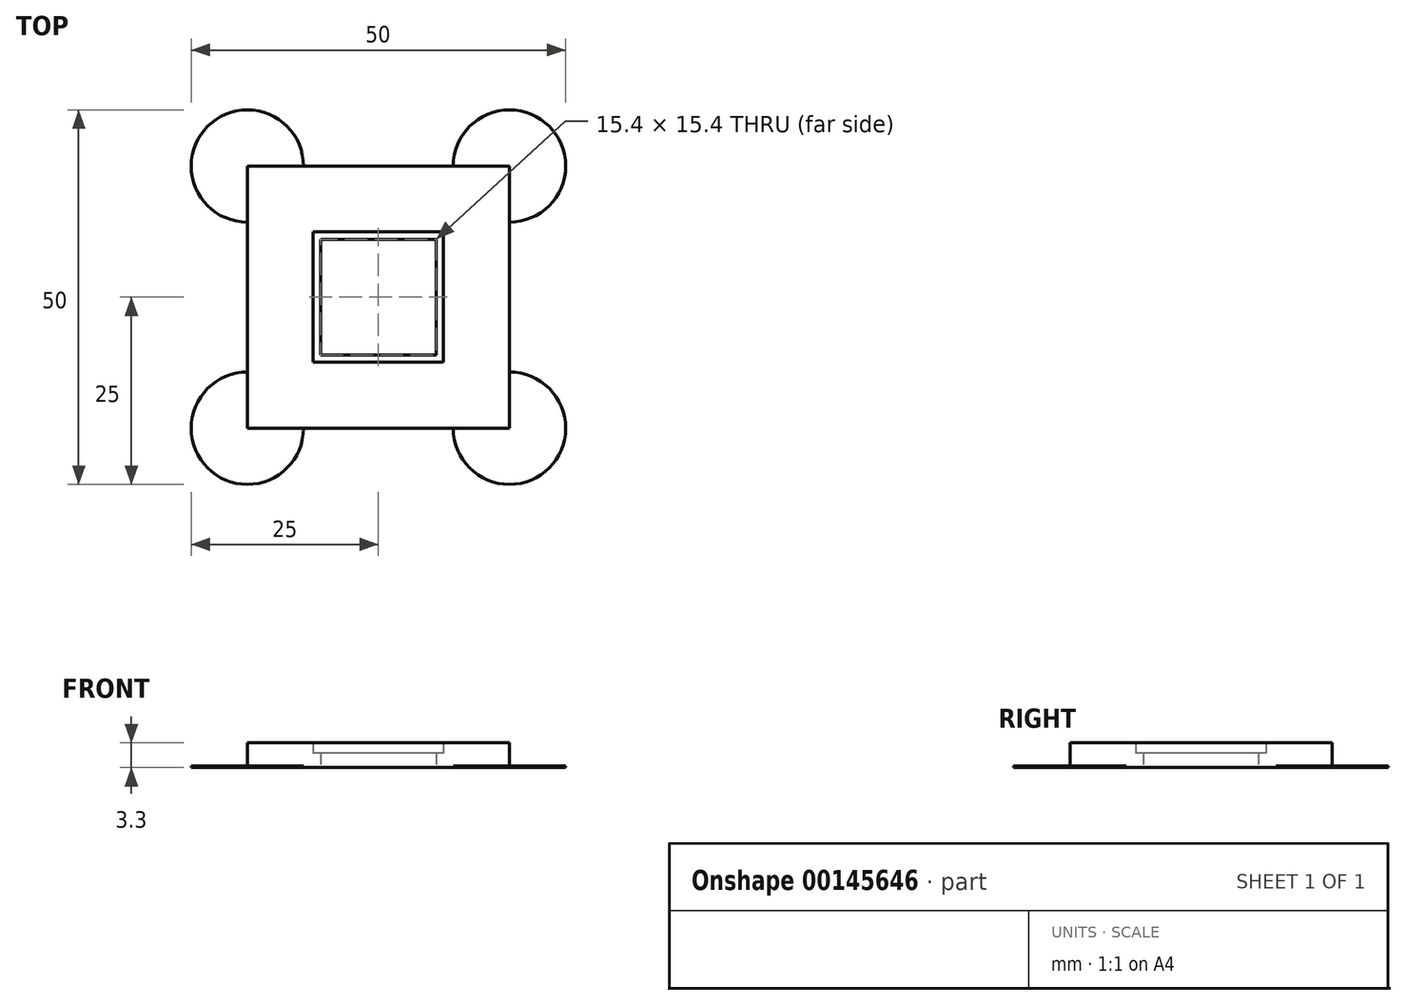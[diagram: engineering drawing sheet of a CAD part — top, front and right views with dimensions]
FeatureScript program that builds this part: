
annotation { "Feature Type Name" : "Feature", "Feature Type Description" : "" }
export const myFeature = defineFeature(function(context is Context, id is Id, definition is map)
    precondition{}
    {
        {
            var Q0;
            Q0=qCreatedBy(makeId("Top.planeOp"),FACE);
            var sketch = newSketch(context, id + "F0", { "sketchPlane" : qUnion([Q0])});
            skLineSegment(sketch, "E0.bottom", {"start": v(17.5, 17.5) * mm, "end": v(-17.5, 17.5) * mm});
            skLineSegment(sketch, "E0.top", {"start": v(17.5, -17.5) * mm, "end": v(-17.5, -17.5) * mm});
            skLineSegment(sketch, "E0.left", {"start": v(17.5, 17.5) * mm, "end": v(17.5, -17.5) * mm});
            skLineSegment(sketch, "E0.right", {"start": v(-17.5, 17.5) * mm, "end": v(-17.5, -17.5) * mm});
            skPoint(sketch, "E0.middle", {"position": v(0, 0) * mm});
            skLineSegment(sketch, "E1.bottom", {"start": v(7.7, 7.7) * mm, "end": v(-7.7, 7.7) * mm});
            skLineSegment(sketch, "E1.top", {"start": v(7.7, -7.7) * mm, "end": v(-7.7, -7.7) * mm});
            skLineSegment(sketch, "E1.left", {"start": v(7.7, 7.7) * mm, "end": v(7.7, -7.7) * mm});
            skLineSegment(sketch, "E1.right", {"start": v(-7.7, 7.7) * mm, "end": v(-7.7, -7.7) * mm});
            skLineSegment(sketch, "E2.bottom", {"start": v(8.7, 8.7) * mm, "end": v(-8.7, 8.7) * mm});
            skLineSegment(sketch, "E2.top", {"start": v(8.7, -8.7) * mm, "end": v(-8.7, -8.7) * mm});
            skLineSegment(sketch, "E2.left", {"start": v(8.7, 8.7) * mm, "end": v(8.7, -8.7) * mm});
            skLineSegment(sketch, "E2.right", {"start": v(-8.7, 8.7) * mm, "end": v(-8.7, -8.7) * mm});
            skSolve(sketch);
        }
        {
            var Q0;
            Q0=makeQuery(id+"F0.imprint","IMPRINT",FACE,{"disambiguationData":[TD([[makeQuery(id+"F0.imprint","IMPRINT",EDGE,{"derivedFrom":sQuery(id+"F0.wireOp",EDGE,"E1.bottom")}),-1.0]])]});
            extrude(context, id + "F5", {"entities" : qUnion([Q0]), "depth" : 1.9 * mm});
        }
        {
            var Q0;
            Q0=makeQuery(id+"F0.imprint","IMPRINT",FACE,{"disambiguationData":[TD([[makeQuery(id+"F0.imprint","IMPRINT",EDGE,{"derivedFrom":sQuery(id+"F0.wireOp",EDGE,"E0.bottom")}),1.0]])]});
            var Q1;
            Q1=makeQuery(id+"F5.opExtrude","CAP_FACE",FACE,{"disambiguationData":[OSD([sQuery(id+"F0.wireOp",EDGE,"E1.bottom"),sQuery(id+"F0.wireOp",EDGE,"E1.top"),sQuery(id+"F0.wireOp",EDGE,"E1.left"),sQuery(id+"F0.wireOp",EDGE,"E1.right"),sQuery(id+"F0.wireOp",EDGE,"E2.bottom"),sQuery(id+"F0.wireOp",EDGE,"E2.top"),sQuery(id+"F0.wireOp",EDGE,"E2.left"),sQuery(id+"F0.wireOp",EDGE,"E2.right")])],"isStart":false});
            extrude(context, id + "F1", {"entities" : qUnion([Q0]), "endBound" : BoundingType.UP_TO_SURFACE, "endBoundEntityFace" : qUnion([Q1]), "depth" : 2 * mm});
        }
        {
            var Q0;
            Q0=makeQuery(id+"F1.opExtrude","CAP_FACE",FACE,{"disambiguationData":[OSD([sQuery(id+"F0.wireOp",EDGE,"E1.bottom"),sQuery(id+"F0.wireOp",EDGE,"E1.top"),sQuery(id+"F0.wireOp",EDGE,"E1.left"),sQuery(id+"F0.wireOp",EDGE,"E1.right"),sQuery(id+"F0.wireOp",EDGE,"E2.bottom"),sQuery(id+"F0.wireOp",EDGE,"E2.top"),sQuery(id+"F0.wireOp",EDGE,"E2.left"),sQuery(id+"F0.wireOp",EDGE,"E2.right")])],"isStart":false});
            extrude(context, id + "F2", {"entities" : qUnion([Q0]), "operationType" : NewBodyOperationType.ADD, "depth" : 1.4 * mm});
        }
        {
            var Q0;
            Q0=qCreatedBy(makeId("Top.planeOp"),FACE);
            var sketch = newSketch(context, id + "F3", { "sketchPlane" : qUnion([Q0])});
            skLineSegment(sketch, "E3.0.0", {"start": v(17.5, -17.5) * mm, "end": v(17.5, 17.5) * mm, "construction": true});
            skLineSegment(sketch, "E3.0.1", {"start": v(17.5, 17.5) * mm, "end": v(-17.5, 17.5) * mm, "construction": true});
            skLineSegment(sketch, "E3.0.2", {"start": v(-17.5, 17.5) * mm, "end": v(-17.5, -17.5) * mm, "construction": true});
            skLineSegment(sketch, "E3.0.3", {"start": v(-17.5, -17.5) * mm, "end": v(17.5, -17.5) * mm, "construction": true});
            skCircle(sketch, "E4", {"center": v(17.5, 17.5) * mm, "radius": 7.5 * mm});
            skCircle(sketch, "E5", {"center": v(-17.5, 17.5) * mm, "radius": 7.5 * mm});
            skCircle(sketch, "E6", {"center": v(-17.5, -17.5) * mm, "radius": 7.5 * mm});
            skCircle(sketch, "E7", {"center": v(17.5, -17.5) * mm, "radius": 7.5 * mm});
            skSolve(sketch);
        }
        {
            var Q0;
            Q0 = qSketchRegion(id + "F3", true);
            extrude(context, id + "F4", {"entities" : qUnion([Q0]), "operationType" : NewBodyOperationType.ADD, "depth" : .2064 * mm});
        }
    });
